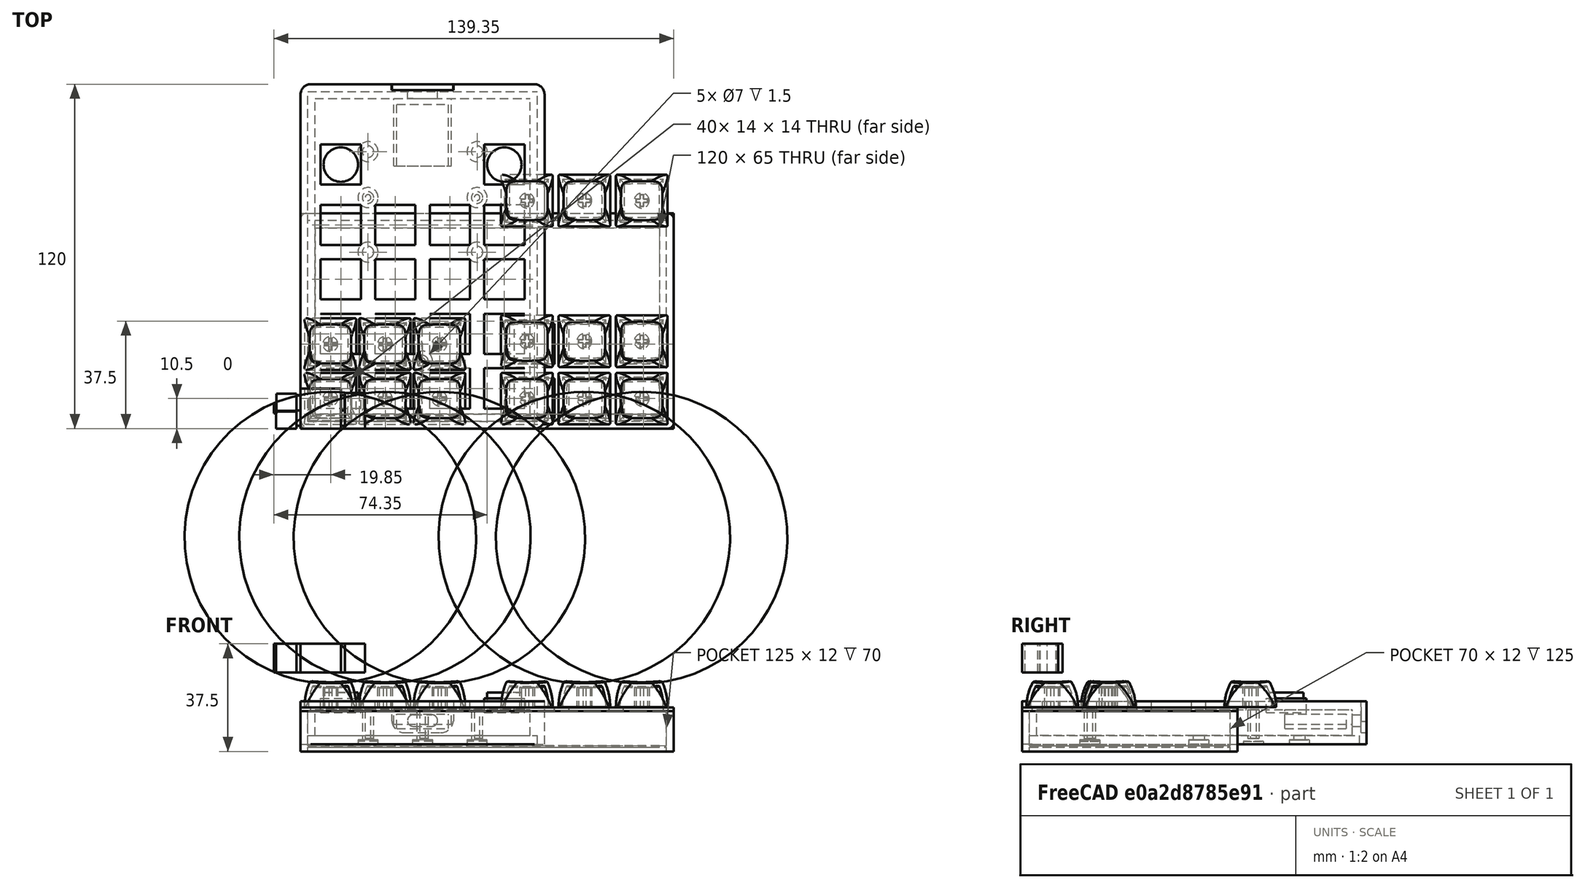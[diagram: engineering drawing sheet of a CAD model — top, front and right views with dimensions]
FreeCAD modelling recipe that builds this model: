
FCSTD DOCUMENT  (FreeCAD 1.0R39109 (Git))
Label: control-v0.8
License: All rights reserved
LicenseURL: https://en.wikipedia.org/wiki/All_rights_reserved
objects: Part::Box×54, Part::Cut×46, Part::Cylinder×25, Part::Feature×15, App::DocumentObjectGroup×7, Part::Fillet×3, Part::MultiFuse×2, Part::FeaturePython×1
note: 146 computed .brp shape members not serialized (recipe doc carries the construction recipe); baked Part::Feature solids carry a one-line shape summary decoded from their .brp

FEATURE [Part::Box] Box  label="Upper Housing"
  AttacherType = Attacher::AttachEngine3D
  Height = 1.35
  Length = 130
  Placement = pos=(0,0,11.5) rot=(0,0,1;0rad)
  Width = 75
FEATURE [Part::Box] Box001  label="Cube"
  AttacherType = Attacher::AttachEngine3D
  Height = 4
  Length = 14
  Placement = pos=(3.5,3.5,10) rot=(0,0,1;0rad)
  Width = 14
FEATURE [Part::Box] Box002  label="Cube001"
  AttacherType = Attacher::AttachEngine3D
  Height = 4
  Length = 14
  Placement = pos=(3.5,22.5,10) rot=(0,0,1;0rad)
  Width = 14
FEATURE [Part::Box] Box003  label="Cube002"
  AttacherType = Attacher::AttachEngine3D
  Height = 4
  Length = 14
  Placement = pos=(22.5,22.5,10) rot=(0,0,1;0rad)
  Width = 14
FEATURE [Part::Box] Box005  label="Cube004"
  AttacherType = Attacher::AttachEngine3D
  Height = 4
  Length = 14
  Placement = pos=(41.5,3.5,10) rot=(0,0,1;0rad)
  Width = 14
FEATURE [Part::Box] Box006  label="Cube005"
  AttacherType = Attacher::AttachEngine3D
  Height = 4
  Length = 14
  Placement = pos=(41.5,22.5,10) rot=(0,0,1;0rad)
  Width = 14
FEATURE [Part::Box] Box007  label="Cube006"
  AttacherType = Attacher::AttachEngine3D
  Height = 4
  Length = 14
  Placement = pos=(112.5,3.5,10) rot=(0,0,1;0rad)
  Width = 14
FEATURE [Part::Box] Box008  label="Cube007"
  AttacherType = Attacher::AttachEngine3D
  Height = 4
  Length = 14
  Placement = pos=(93.5,3.5,10) rot=(0,0,1;0rad)
  Width = 14
FEATURE [Part::Box] Box009  label="Cube008"
  AttacherType = Attacher::AttachEngine3D
  Height = 4
  Length = 14
  Placement = pos=(74.5,3.5,10) rot=(0,0,1;0rad)
  Width = 14
FEATURE [Part::Box] Box010  label="Cube009"
  AttacherType = Attacher::AttachEngine3D
  Height = 4
  Length = 14
  Placement = pos=(74.5,22.5,10) rot=(0,0,1;0rad)
  Width = 14
FEATURE [Part::Box] Box011  label="Cube010"
  AttacherType = Attacher::AttachEngine3D
  Height = 4
  Length = 14
  Placement = pos=(93.5,22.5,10) rot=(0,0,1;0rad)
  Width = 14
FEATURE [Part::Box] Box012  label="Cube011"
  AttacherType = Attacher::AttachEngine3D
  Height = 4
  Length = 14
  Placement = pos=(112.5,22.5,10) rot=(0,0,1;0rad)
  Width = 14
FEATURE [Part::Cylinder] Cylinder  label="Small Knob"
  Angle = 360
  AttacherType = Attacher::AttachEngine3D
  FirstAngle = 0
  Height = 3
  Placement = pos=(14,92,15) rot=(0,0,1;0rad)
  Radius = 6
  SecondAngle = 0
FEATURE [Part::Feature] Part__Feature  label="1u v2"
  Placement = pos=(21.5,15,13) rot=(1,0,0;1.5708rad)
  shape: bbox 18 x 18.01 x 11.79 mm, 51 faces (baked)
FEATURE [Part::Box] Box004  label="Cube003"
  AttacherType = Attacher::AttachEngine3D
  Height = 4
  Length = 14
  Placement = pos=(22.5,3.5,10) rot=(0,0,1;0rad)
  Width = 14
FEATURE [Part::Feature] Part__Feature001  label="1u v003"
  Placement = pos=(40.5,15,13) rot=(1,0,0;1.5708rad)
  shape: bbox 18 x 18.01 x 11.79 mm, 51 faces (baked)
FEATURE [Part::Feature] Part__Feature002  label="1u v004"
  Placement = pos=(59.5,15,13) rot=(1,0,0;1.5708rad)
  shape: bbox 18 x 18.01 x 11.79 mm, 51 faces (baked)
FEATURE [Part::Feature] Part__Feature003  label="1u v005"
  Placement = pos=(59.5,34,13) rot=(1,0,0;1.5708rad)
  shape: bbox 18 x 18.01 x 11.79 mm, 51 faces (baked)
FEATURE [Part::Feature] Part__Feature004  label="1u v006"
  Placement = pos=(21.5,34,13) rot=(1,0,0;1.5708rad)
  shape: bbox 18 x 18.01 x 11.79 mm, 51 faces (baked)
FEATURE [Part::Feature] Part__Feature005  label="1u v007"
  Placement = pos=(40.5,34,13) rot=(1,0,0;1.5708rad)
  shape: bbox 18 x 18.01 x 11.79 mm, 51 faces (baked)
FEATURE [Part::Feature] Part__Feature006  label="1u v008"
  Placement = pos=(90,35,13) rot=(1,0,0;1.5708rad)
  shape: bbox 18 x 18.01 x 11.79 mm, 51 faces (baked)
FEATURE [Part::Feature] Part__Feature007  label="1u v009"
  Placement = pos=(90,15,13) rot=(1,0,0;1.5708rad)
  shape: bbox 18 x 18.01 x 11.79 mm, 51 faces (baked)
FEATURE [Part::Feature] Part__Feature008  label="1u v010"
  Placement = pos=(110,15,13) rot=(1,0,0;1.5708rad)
  shape: bbox 18 x 18.01 x 11.79 mm, 51 faces (baked)
FEATURE [Part::Feature] Part__Feature009  label="1u v011"
  Placement = pos=(110,35,13) rot=(1,0,0;1.5708rad)
  shape: bbox 18 x 18.01 x 11.79 mm, 51 faces (baked)
FEATURE [Part::Feature] Part__Feature010  label="1u v012"
  Placement = pos=(130,15,13) rot=(1,0,0;1.5708rad)
  shape: bbox 18 x 18.01 x 11.79 mm, 51 faces (baked)
FEATURE [Part::Feature] Part__Feature011  label="1u v013"
  Placement = pos=(130,35,13) rot=(1,0,0;1.5708rad)
  shape: bbox 18 x 18.01 x 11.79 mm, 51 faces (baked)
FEATURE [Part::Feature] Part__Feature012  label="1u v014"
  Placement = pos=(130,84,13) rot=(1,0,0;1.5708rad)
  shape: bbox 18 x 18.01 x 11.79 mm, 51 faces (baked)
FEATURE [Part::Feature] Part__Feature013  label="1u v015"
  Placement = pos=(110,84,13) rot=(1,0,0;1.5708rad)
  shape: bbox 18 x 18.01 x 11.79 mm, 51 faces (baked)
FEATURE [Part::Feature] Part__Feature014  label="1u v016"
  Placement = pos=(90,84,13) rot=(1,0,0;1.5708rad)
  shape: bbox 18 x 18.01 x 11.79 mm, 51 faces (baked)
FEATURE [App::DocumentObjectGroup] Group004  label="Keycaps"
  Group = -> [Part__Feature,Part__Feature001,Part__Feature002,Part__Feature004,Part__Feature005,Part__Feature003,Part__Feature007,Part__Feature008,Part__Feature010,Part__Feature006,Part__Feature009,Part__Feature011,Part__Feature012,Part__Feature013,Part__Feature014]
FEATURE [Part::Cut] Cut
  Base = -> Box
  Tool = -> Box001
FEATURE [Part::Cut] Cut001
  Base = -> Cut
  Tool = -> Box004
FEATURE [Part::Cut] Cut002
  Base = -> Cut001
  Tool = -> Box005
FEATURE [Part::Cut] Cut003
  Base = -> Cut002
  Tool = -> Box002
FEATURE [Part::Cut] Cut004
  Base = -> Cut003
  Tool = -> Box003
FEATURE [Part::Cut] Cut005
  Base = -> Cut004
  Tool = -> Box006
FEATURE [Part::Cut] Cut006
  Base = -> Cut005
  Tool = -> Box009
FEATURE [Part::Cut] Cut007
  Base = -> Cut006
  Tool = -> Box008
FEATURE [Part::Cut] Cut008
  Base = -> Cut007
  Tool = -> Box007
FEATURE [Part::Cut] Cut009
  Base = -> Cut008
  Tool = -> Box010
FEATURE [Part::Cut] Cut010
  Base = -> Cut009
  Tool = -> Box011
FEATURE [Part::Cut] Cut011
  Base = -> Cut010
  Tool = -> Box012
FEATURE [App::DocumentObjectGroup] Group001  label="Upper Housing2"
  Group = -> [Cut011]
FEATURE [Part::Box] Box016  label="Cube015"
  AttacherType = Attacher::AttachEngine3D
  Height = 15
  Length = 130
  Placement = pos=(0,0,-13.5) rot=(0,0,1;0rad)
  Width = 75
FEATURE [Part::Box] Box017  label="Cube016"
  AttacherType = Attacher::AttachEngine3D
  Height = 17.5
  Length = 125
  Placement = pos=(2.5,2.5,-11.5) rot=(0,0,1;0rad)
  Width = 70
FEATURE [Part::Cut] Cut012
  Base = -> Box016
  Placement = pos=(0,0,11) rot=(0,0,1;0rad)
  Tool = -> Box017
FEATURE [Part::Box] Box019  label="Cube018"
  AttacherType = Attacher::AttachEngine3D
  Height = 10
  Length = 14
  Placement = pos=(0,0,25) rot=(0,0,1;0rad)
  Width = 14
FEATURE [Part::Box] Box020  label="Cube019"
  AttacherType = Attacher::AttachEngine3D
  Height = 10
  Length = 1.35
  Placement = pos=(14,6.35,25) rot=(0,0,1;0rad)
  Width = 5.35
FEATURE [Part::Box] Box021  label="Cube020"
  AttacherType = Attacher::AttachEngine3D
  Height = 10
  Length = 1.4
  Placement = pos=(14,1,25) rot=(0,0,1;0rad)
  Width = 5.35
FEATURE [Part::Box] Box022  label="Cube021"
  AttacherType = Attacher::AttachEngine3D
  Height = 10
  Length = 1.45
  Placement = pos=(-1.45,6.35,25) rot=(0,0,1;0rad)
  Width = 5.35
FEATURE [Part::Box] Box023  label="Cube022"
  AttacherType = Attacher::AttachEngine3D
  Height = 10
  Length = 1.5
  Placement = pos=(-1.5,1,25) rot=(0,0,1;0rad)
  Width = 5.35
FEATURE [Part::Box] Box024  label="Cube023"
  AttacherType = Attacher::AttachEngine3D
  Height = 10
  Length = 7
  Placement = pos=(-8.45,6,25) rot=(0,0,1;0rad)
  Width = 6.22
FEATURE [Part::Box] Box025  label="Cube024"
  AttacherType = Attacher::AttachEngine3D
  Height = 10
  Length = 0.9
  Placement = pos=(-9.35,5.35,25) rot=(0,0,1;0rad)
  Width = 3.3
FEATURE [Part::Box] Box026  label="Cube025"
  AttacherType = Attacher::AttachEngine3D
  Height = 10
  Length = 7
  Placement = pos=(15.4,0,25) rot=(0,0,1;0rad)
  Width = 12.45
FEATURE [Part::Box] Box027  label="Cube026"
  AttacherType = Attacher::AttachEngine3D
  Height = 10
  Length = 7
  Placement = pos=(-8.5,0,25) rot=(0,0,1;0rad)
  Width = 6.22
FEATURE [App::DocumentObjectGroup] Group  label="Stab"
  Group = -> [Box019,Box022,Box021,Box023,Box024,Box027,Box025,Box026,Box020]
FEATURE [Part::Box] Box028  label="Cube027"
  AttacherType = Attacher::AttachEngine3D
  Height = 10
  Length = 125
  Placement = pos=(2.5,2.5,-11) rot=(0,0,1;0rad)
  Width = 70
FEATURE [Part::Box] Box029  label="Cube028"
  AttacherType = Attacher::AttachEngine3D
  Height = 14
  Length = 120
  Placement = pos=(5,5,-2.5) rot=(0,0,1;0rad)
  Width = 65
FEATURE [Part::Cut] Cut013
  Base = -> Cut012
  Tool = -> Box029
FEATURE [Part::Cut] Cut014
  Base = -> Cut013
  Tool = -> Box028
FEATURE [Part::FeaturePython] Connect  label="Upper Housing003"  # WARN: FeaturePython — macro-defined, semantics opaque (R4)
  Objects = -> [Group001,Cut014]
  Tolerance = 0
FEATURE [Part::Fillet] Fillet
  Base = -> Connect
  EdgeLinks = -> Connect [Edge5,Edge7,Edge13,Edge14,Edge50,Edge52,Edge102,Edge104,Edge141,Edge150,Edge203,Edge204]
  Edges = 12 edges r=2: [Edge5,Edge7,Edge13,Edge14,Edge50,Edge52,Edge102,Edge104,Edge141,Edge150,Edge203,Edge204]
FEATURE [Part::Box] Box031  label="Cube029"
  AttacherType = Attacher::AttachEngine3D
  Height = 15
  Length = 85
  Width = 120
FEATURE [Part::Box] Box032  label="Cube030"
  AttacherType = Attacher::AttachEngine3D
  Height = 10
  Length = 14
  Placement = pos=(7,7,6) rot=(0,0,1;0rad)
  Width = 14
FEATURE [Part::Box] Box033  label="Cube031"
  AttacherType = Attacher::AttachEngine3D
  Height = 10
  Length = 14
  Placement = pos=(26,7,6) rot=(0,0,1;0rad)
  Width = 14
FEATURE [Part::Box] Box034  label="Cube032"
  AttacherType = Attacher::AttachEngine3D
  Height = 10
  Length = 14
  Placement = pos=(45,7,6) rot=(0,0,1;0rad)
  Width = 14
FEATURE [Part::Box] Box035  label="Cube033"
  AttacherType = Attacher::AttachEngine3D
  Height = 10
  Length = 14
  Placement = pos=(64,7,6) rot=(0,0,1;0rad)
  Width = 14
FEATURE [Part::Box] Box036  label="Cube034"
  AttacherType = Attacher::AttachEngine3D
  Height = 10
  Length = 14
  Placement = pos=(7,26,6) rot=(0,0,1;0rad)
  Width = 14
FEATURE [Part::Box] Box037  label="Cube035"
  AttacherType = Attacher::AttachEngine3D
  Height = 10
  Length = 14
  Placement = pos=(26,26,6) rot=(0,0,1;0rad)
  Width = 14
FEATURE [Part::Box] Box038  label="Cube036"
  AttacherType = Attacher::AttachEngine3D
  Height = 10
  Length = 14
  Placement = pos=(45,26,6) rot=(0,0,1;0rad)
  Width = 14
FEATURE [Part::Box] Box039  label="Cube037"
  AttacherType = Attacher::AttachEngine3D
  Height = 10
  Length = 14
  Placement = pos=(64,26,6) rot=(0,0,1;0rad)
  Width = 14
FEATURE [Part::Box] Box040  label="Cube038"
  AttacherType = Attacher::AttachEngine3D
  Height = 10
  Length = 14
  Placement = pos=(7,45,6) rot=(0,0,1;0rad)
  Width = 14
FEATURE [Part::Box] Box041  label="Cube039"
  AttacherType = Attacher::AttachEngine3D
  Height = 10
  Length = 14
  Placement = pos=(26,45,6) rot=(0,0,1;0rad)
  Width = 14
FEATURE [Part::Box] Box042  label="Cube040"
  AttacherType = Attacher::AttachEngine3D
  Height = 10
  Length = 14
  Placement = pos=(45,45,6) rot=(0,0,1;0rad)
  Width = 14
FEATURE [Part::Box] Box043  label="Cube041"
  AttacherType = Attacher::AttachEngine3D
  Height = 10
  Length = 14
  Placement = pos=(64,45,6) rot=(0,0,1;0rad)
  Width = 14
FEATURE [Part::Box] Box044  label="Cube042"
  AttacherType = Attacher::AttachEngine3D
  Height = 10
  Length = 14
  Placement = pos=(7,64,6) rot=(0,0,1;0rad)
  Width = 14
FEATURE [Part::Box] Box045  label="Cube043"
  AttacherType = Attacher::AttachEngine3D
  Height = 10
  Length = 14
  Placement = pos=(26,64,6) rot=(0,0,1;0rad)
  Width = 14
FEATURE [Part::Box] Box046  label="Cube044"
  AttacherType = Attacher::AttachEngine3D
  Height = 10
  Length = 14
  Placement = pos=(45,64,6) rot=(0,0,1;0rad)
  Width = 14
FEATURE [Part::Box] Box047  label="Cube045"
  AttacherType = Attacher::AttachEngine3D
  Height = 10
  Length = 14
  Placement = pos=(64,64,6) rot=(0,0,1;0rad)
  Width = 14
FEATURE [Part::Box] Box049  label="Cube047"
  AttacherType = Attacher::AttachEngine3D
  Height = 12
  Length = 75
  Placement = pos=(5,5,0) rot=(0,0,1;0rad)
  Width = 110
FEATURE [Part::Box] Box050  label="Lower Housing"
  AttacherType = Attacher::AttachEngine3D
  Height = 3
  Length = 80
  Placement = pos=(2.5,2.5,0) rot=(0,0,1;0rad)
  Width = 115
FEATURE [Part::Box] Box051  label="Cube049"
  AttacherType = Attacher::AttachEngine3D
  Height = 3
  Length = 80
  Placement = pos=(2.5,2.5,0) rot=(0,0,1;0rad)
  Width = 115
FEATURE [Part::Cut] Cut015
  Base = -> Box031
  Tool = -> Box049
FEATURE [Part::Cut] Cut016
  Base = -> Cut015
  Tool = -> Box051
FEATURE [Part::Cut] Cut017
  Base = -> Cut016
  Tool = -> Box032
FEATURE [Part::Cut] Cut018
  Base = -> Cut017
  Tool = -> Box033
FEATURE [Part::Cut] Cut019
  Base = -> Cut018
  Tool = -> Box034
FEATURE [Part::Cut] Cut020
  Base = -> Cut019
  Tool = -> Box035
FEATURE [Part::Cut] Cut021
  Base = -> Cut020
  Tool = -> Box036
FEATURE [Part::Cut] Cut022
  Base = -> Cut021
  Tool = -> Box037
FEATURE [Part::Cut] Cut023
  Base = -> Cut022
  Tool = -> Box038
FEATURE [Part::Cut] Cut024
  Base = -> Cut023
  Tool = -> Box039
FEATURE [Part::Cut] Cut025
  Base = -> Cut024
  Tool = -> Box040
FEATURE [Part::Cut] Cut026
  Base = -> Cut025
  Tool = -> Box041
FEATURE [Part::Cut] Cut027
  Base = -> Cut026
  Tool = -> Box042
FEATURE [Part::Cut] Cut028
  Base = -> Cut027
  Tool = -> Box043
FEATURE [Part::Cut] Cut029
  Base = -> Cut028
  Tool = -> Box044
FEATURE [Part::Cut] Cut030
  Base = -> Cut029
  Tool = -> Box045
FEATURE [Part::Cut] Cut031
  Base = -> Cut030
  Tool = -> Box046
FEATURE [Part::Cut] Cut032
  Base = -> Cut031
  Tool = -> Box047
FEATURE [App::DocumentObjectGroup] Group005  label="Switch Slots"
  Group = -> [Cut032]
FEATURE [Part::Fillet] Fillet001
  Base = -> Cut032
  EdgeLinks = -> Cut032 [Edge1]
  Edges = 1 edges r=3.5: [Edge1]
FEATURE [Part::Fillet] Fillet002
  Base = -> Fillet001
  EdgeLinks = -> Fillet001 [Edge3,Edge76,Edge83]
  Edges = 3 edges r=3.5: [Edge3,Edge76,Edge83]
FEATURE [Part::Cylinder] Cylinder004
  Angle = 360
  AttacherType = Attacher::AttachEngine3D
  FirstAngle = 0
  Height = 10
  Placement = pos=(42.5,23.5,2) rot=(0,0,1;0rad)
  Radius = 2
  SecondAngle = 0
FEATURE [Part::Cylinder] Cylinder005
  Angle = 360
  AttacherType = Attacher::AttachEngine3D
  FirstAngle = 0
  Height = 10
  Placement = pos=(61.5,80.5,2) rot=(0,0,1;0rad)
  Radius = 2
  SecondAngle = 0
FEATURE [Part::Cylinder] Cylinder006
  Angle = 360
  AttacherType = Attacher::AttachEngine3D
  FirstAngle = 0
  Height = 10
  Placement = pos=(23.5,80.5,2) rot=(0,0,1;0rad)
  Radius = 2
  SecondAngle = 0
FEATURE [App::DocumentObjectGroup] Group006  label="Screw Posts"
  Group = -> [Cylinder004,Cylinder005,Cylinder006]
FEATURE [Part::Cylinder] Cylinder009
  Angle = 360
  AttacherType = Attacher::AttachEngine3D
  FirstAngle = 0
  Height = 15
  Placement = pos=(42.5,23.5,-13.5) rot=(0,0,1;0rad)
  Radius = 3.5
  SecondAngle = 0
FEATURE [Part::Cylinder] Cylinder010
  Angle = 360
  AttacherType = Attacher::AttachEngine3D
  FirstAngle = 0
  Height = 15
  Placement = pos=(61.5,61.5,-13.5) rot=(0,0,1;0rad)
  Radius = 3.5
  SecondAngle = 0
FEATURE [Part::Cylinder] Cylinder011
  Angle = 360
  AttacherType = Attacher::AttachEngine3D
  FirstAngle = 0
  Height = 15
  Placement = pos=(23.5,61.5,-13.5) rot=(0,0,1;0rad)
  Radius = 3.5
  SecondAngle = 0
FEATURE [Part::Cylinder] Cylinder012
  Angle = 360
  AttacherType = Attacher::AttachEngine3D
  FirstAngle = 0
  Height = 15
  Placement = pos=(61.5,96.5,-13.5) rot=(0,0,1;0rad)
  Radius = 3.5
  SecondAngle = 0
FEATURE [Part::Cylinder] Cylinder013
  Angle = 360
  AttacherType = Attacher::AttachEngine3D
  FirstAngle = 0
  Height = 15
  Placement = pos=(23.5,96.5,-13.5) rot=(0,0,1;0rad)
  Radius = 3.5
  SecondAngle = 0
FEATURE [Part::Cut] Cut033
  Base = -> Box050
  Tool = -> Cylinder009
FEATURE [Part::Cut] Cut034
  Base = -> Cut033
  Tool = -> Cylinder010
FEATURE [Part::Cut] Cut035
  Base = -> Cut034
  Tool = -> Cylinder011
FEATURE [Part::Cut] Cut036
  Base = -> Cut035
  Tool = -> Cylinder012
FEATURE [Part::Cut] Cut037
  Base = -> Cut036
  Tool = -> Cylinder013
FEATURE [Part::Cylinder] Cylinder014
  Angle = 360
  AttacherType = Attacher::AttachEngine3D
  FirstAngle = 0
  Height = 15
  Placement = pos=(42.5,23.5,-3) rot=(0,0,1;0rad)
  Radius = 2
  SecondAngle = 0
FEATURE [Part::Cylinder] Cylinder015
  Angle = 360
  AttacherType = Attacher::AttachEngine3D
  FirstAngle = 0
  Height = 15
  Placement = pos=(61.5,61.5,-3) rot=(0,0,1;0rad)
  Radius = 2
  SecondAngle = 0
FEATURE [Part::Cylinder] Cylinder016
  Angle = 360
  AttacherType = Attacher::AttachEngine3D
  FirstAngle = 0
  Height = 15
  Placement = pos=(23.5,61.5,-3) rot=(0,0,1;0rad)
  Radius = 2
  SecondAngle = 0
FEATURE [Part::Cylinder] Cylinder017
  Angle = 360
  AttacherType = Attacher::AttachEngine3D
  FirstAngle = 0
  Height = 15
  Placement = pos=(61.5,96.5,-3) rot=(0,0,1;0rad)
  Radius = 2
  SecondAngle = 0
FEATURE [Part::Cylinder] Cylinder018
  Angle = 360
  AttacherType = Attacher::AttachEngine3D
  FirstAngle = 0
  Height = 15
  Placement = pos=(23.5,96.5,-3) rot=(0,0,1;0rad)
  Radius = 2
  SecondAngle = 0
FEATURE [Part::Cut] Cut038
  Base = -> Cut037
  Tool = -> Cylinder014
FEATURE [Part::Cut] Cut039
  Base = -> Cut038
  Tool = -> Cylinder015
FEATURE [Part::Cut] Cut040
  Base = -> Cut039
  Tool = -> Cylinder016
FEATURE [Part::Cut] Cut041
  Base = -> Cut040
  Tool = -> Cylinder017
FEATURE [Part::Cut] Cut042
  Base = -> Cut041
  Tool = -> Cylinder018
FEATURE [Part::Cylinder] Cylinder019
  Angle = 360
  AttacherType = Attacher::AttachEngine3D
  FirstAngle = 0
  Height = 10
  Placement = pos=(42.5,23.5,2) rot=(0,0,1;0rad)
  Radius = 1
  SecondAngle = 0
FEATURE [Part::Cylinder] Cylinder020
  Angle = 360
  AttacherType = Attacher::AttachEngine3D
  FirstAngle = 0
  Height = 1
  Placement = pos=(42.5,23.5,0) rot=(0,0,1;0rad)
  Radius = 3.5
  SecondAngle = 0
FEATURE [Part::Cylinder] Cylinder021
  Angle = 360
  AttacherType = Attacher::AttachEngine3D
  FirstAngle = 0
  Height = 10
  Placement = pos=(61.5,80.5,2) rot=(0,0,1;0rad)
  Radius = 1
  SecondAngle = 0
FEATURE [Part::Cylinder] Cylinder022
  Angle = 360
  AttacherType = Attacher::AttachEngine3D
  FirstAngle = 0
  Height = 1
  Placement = pos=(61.5,80.5,0) rot=(0,0,1;0rad)
  Radius = 3.5
  SecondAngle = 0
FEATURE [Part::Cylinder] Cylinder023
  Angle = 360
  AttacherType = Attacher::AttachEngine3D
  FirstAngle = 0
  Height = 10
  Placement = pos=(23.5,80.5,2) rot=(0,0,1;0rad)
  Radius = 1
  SecondAngle = 0
FEATURE [Part::Cylinder] Cylinder024
  Angle = 360
  AttacherType = Attacher::AttachEngine3D
  FirstAngle = 0
  Height = 1
  Placement = pos=(23.5,80.5,0) rot=(0,0,1;0rad)
  Radius = 3.5
  SecondAngle = 0
FEATURE [App::DocumentObjectGroup] Group007  label=""Screws""
  Group = -> [Cylinder019,Cylinder020,Cylinder021,Cylinder022,Cylinder023,Cylinder024]
FEATURE [Part::Box] Box052  label="Cube050"
  AttacherType = Attacher::AttachEngine3D
  Height = 3
  Length = 80
  Placement = pos=(2.5,2.5,0) rot=(0,0,1;0rad)
  Width = 115
FEATURE [Part::Box] Box053  label="rp2040-zero"
  AttacherType = Attacher::AttachEngine3D
  Height = 5
  Length = 20
  Placement = pos=(32.5,91.5,7) rot=(0,0,1;0rad)
  Width = 23.5
FEATURE [Part::Box] Box054  label="rp2040-zero001"
  AttacherType = Attacher::AttachEngine3D
  Height = 5
  Length = 18
  Placement = pos=(33.5,91.5,5.5) rot=(0,0,1;0rad)
  Width = 21.5
FEATURE [Part::Box] Box056  label="Cube052"
  AttacherType = Attacher::AttachEngine3D
  Height = 4
  Length = 6.5
  Placement = pos=(39.25,109,6.25) rot=(0,0,1;0rad)
  Width = 15
FEATURE [Part::Cylinder] Cylinder025
  Angle = 180
  AttacherType = Attacher::AttachEngine3D
  FirstAngle = 0
  Height = 15
  Placement = pos=(39.25,124,8.25) rot=(-0.58,0.58,-0.58;4.18879rad)
  Radius = 2
  SecondAngle = 0
FEATURE [Part::Cylinder] Cylinder026
  Angle = 180
  AttacherType = Attacher::AttachEngine3D
  FirstAngle = 0
  Height = 15
  Placement = pos=(45.75,124,8.25) rot=(-0.58,-0.58,0.58;4.18879rad)
  Radius = 2
  SecondAngle = 0
FEATURE [Part::Box] Box057  label="Cube053"
  AttacherType = Attacher::AttachEngine3D
  Height = 9
  Length = 12.5
  Placement = pos=(36.25,118,4) rot=(0,0,1;0rad)
  Width = 15
FEATURE [Part::Cylinder] Cylinder027
  Angle = 180
  AttacherType = Attacher::AttachEngine3D
  FirstAngle = 0
  Height = 15
  Placement = pos=(36.25,133,8.5) rot=(-0.58,0.58,-0.58;4.18879rad)
  Radius = 4.5
  SecondAngle = 0
FEATURE [Part::Cylinder] Cylinder028
  Angle = 180
  AttacherType = Attacher::AttachEngine3D
  FirstAngle = 0
  Height = 15
  Placement = pos=(48.75,133,8.5) rot=(-0.58,-0.58,0.58;4.18879rad)
  Radius = 4.5
  SecondAngle = 0
FEATURE [Part::MultiFuse] Fusion
  Shapes = -> [Box057,Cylinder027,Cylinder028]
FEATURE [Part::Box] Box058  label="Cube054"
  AttacherType = Attacher::AttachEngine3D
  Height = 10
  Length = 21.5
  Placement = pos=(31.75,118,8) rot=(0,0,1;0rad)
  Width = 10
FEATURE [Part::Cut] Cut043
  Base = -> Fillet002
  Tool = -> Fusion
FEATURE [Part::Cut] Cut044
  Base = -> Cut043
  Tool = -> Box058
FEATURE [Part::MultiFuse] Fusion001
  Shapes = -> [Box056,Cylinder025,Cylinder026]
FEATURE [Part::Cut] Cut045
  Base = -> Cut044
  Tool = -> Fusion001
FEATURE [Part::Box] Box059  label="Cube055"
  AttacherType = Attacher::AttachEngine3D
  Height = 5
  Length = 14
  Placement = pos=(7,85,11) rot=(0,0,1;0rad)
  Width = 14
FEATURE [Part::Box] Box060  label="Cube056"
  AttacherType = Attacher::AttachEngine3D
  Height = 5
  Length = 14
  Placement = pos=(64,85,11) rot=(0,0,1;0rad)
  Width = 14
FEATURE [Part::Cylinder] Cylinder029  label="Small Knob001"
  Angle = 360
  AttacherType = Attacher::AttachEngine3D
  FirstAngle = 0
  Height = 3
  Placement = pos=(71,92,15) rot=(0,0,1;0rad)
  Radius = 6
  SecondAngle = 0
FEATURE [App::DocumentObjectGroup] Group003  label="Rotories"
  Group = -> [Cylinder,Box059,Cylinder029,Box060]
